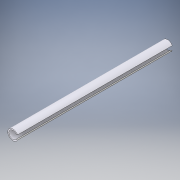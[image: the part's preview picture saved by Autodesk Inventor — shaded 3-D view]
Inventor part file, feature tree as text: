
AUTODESK INVENTOR PART (.ipt)
format: ipt  version: 2017 (Build 210142000, 142)  size: 118,784 bytes
history: native  units: in
note: dims shown in document units (in); Inventor stores cm internally (conversion verified against a paired STEP export)
features: extrude x3, sketch x3, plane x1
ambient origin geometry x8: Origin, YZ Plane, XZ Plane, XY Plane, X Axis, Y Axis, Z Axis, Center Point
bodies: Solid1 (feature_tree)
feature tree (7):
  extrude  "Extrusion1"  Depth=0.813in
  extrude  "Extrusion5"  Depth=15.748in
  plane  "Work Plane2"
  extrude  "Extrusion6"  TaperAngle=0.0deg  [1 undecoded]
  sketch  "Sketch1"  dims[d0=1.0449in d1=0.813in]
  sketch  "Sketch6"  dims[d2=15.748in d3=0.0in d13=0.7874in]
  sketch  "Sketch7"  dims[d14=0.4528in d15=0.0in d16=0.0in d17=0.1575in d19=0.3937in d20=0.0in d21=0.9843in]
note: 1 required parameter value undecoded (feature->parameter linkage not recoverable at this tier; creation-order binding heuristic only, values carry confidence <= 0.55)
